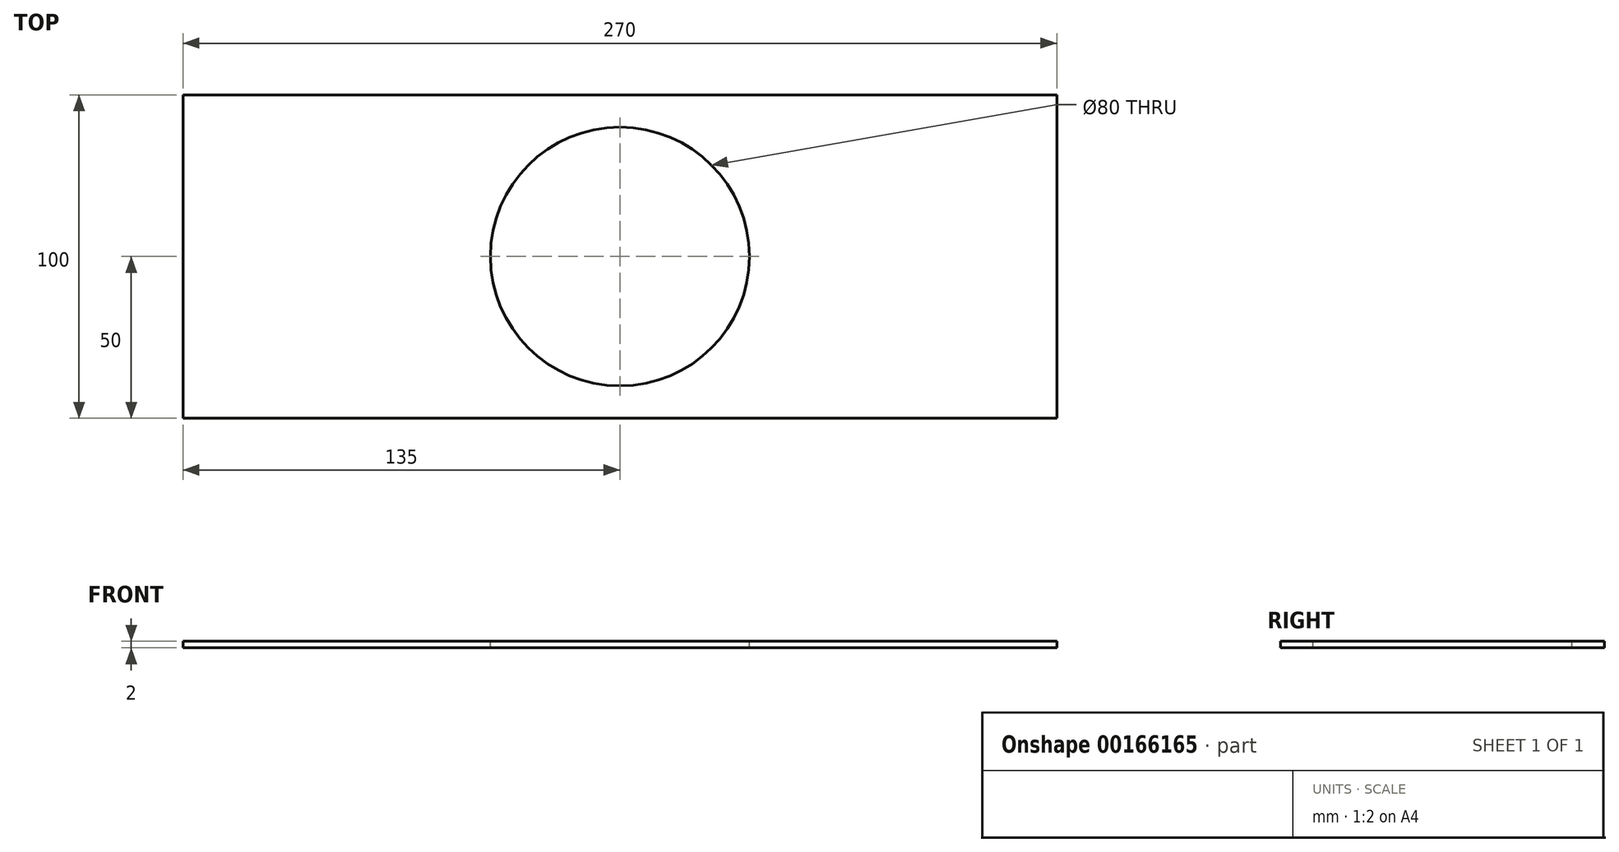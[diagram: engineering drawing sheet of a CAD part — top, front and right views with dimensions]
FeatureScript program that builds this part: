
annotation { "Feature Type Name" : "Feature", "Feature Type Description" : "" }
export const myFeature = defineFeature(function(context is Context, id is Id, definition is map)
    precondition{}
    {
        {
            var Q0;
            Q0=qCreatedBy(makeId("Top.planeOp"),FACE);
            var sketch = newSketch(context, id + "F0", { "sketchPlane" : qUnion([Q0])});
            skLineSegment(sketch, "E0.bottom", {"start": v(135, 50) * mm, "end": v(-135, 50) * mm});
            skLineSegment(sketch, "E0.top", {"start": v(135, -50) * mm, "end": v(-135, -50) * mm});
            skLineSegment(sketch, "E0.left", {"start": v(135, 50) * mm, "end": v(135, -50) * mm});
            skLineSegment(sketch, "E0.right", {"start": v(-135, 50) * mm, "end": v(-135, -50) * mm});
            skPoint(sketch, "E0.middle", {"position": v(0, 0) * mm});
            skSolve(sketch);
        }
        {
            var Q0;
            Q0=makeQuery(id+"F0.imprint","IMPRINT",FACE,{"disambiguationData":[TD([[makeQuery(id+"F0.imprint","IMPRINT",EDGE,{"derivedFrom":sQuery(id+"F0.wireOp",EDGE,"E0.bottom")}),1.0]])]});
            extrude(context, id + "F1", {"entities" : qUnion([Q0]), "depth" : 2 * mm});
        }
        {
            var Q0;
            Q0=makeQuery(id+"F1.opExtrude","CAP_FACE",FACE,{"disambiguationData":[OSD([sQuery(id+"F0.wireOp",EDGE,"E0.bottom"),sQuery(id+"F0.wireOp",EDGE,"E0.top"),sQuery(id+"F0.wireOp",EDGE,"E0.left"),sQuery(id+"F0.wireOp",EDGE,"E0.right")])],"isStart":false});
            var sketch = newSketch(context, id + "F2", { "sketchPlane" : qUnion([Q0])});
            skCircle(sketch, "E1", {"center": v(0, 0) * mm, "radius": 40 * mm});
            skSolve(sketch);
        }
        {
            var Q0;
            Q0=makeQuery(id+"F2.imprint","IMPRINT",FACE,{"disambiguationData":[TD([[makeQuery(id+"F2.imprint","IMPRINT",EDGE,{"derivedFrom":sQuery(id+"F2.wireOp",EDGE,"E1")}),1.0]])]});
            extrude(context, id + "F3", {"entities" : qUnion([Q0]), "operationType" : NewBodyOperationType.REMOVE, "endBound" : BoundingType.THROUGH_ALL, "oppositeDirection" : true, "depth" : 25 * mm});
        }
    });
